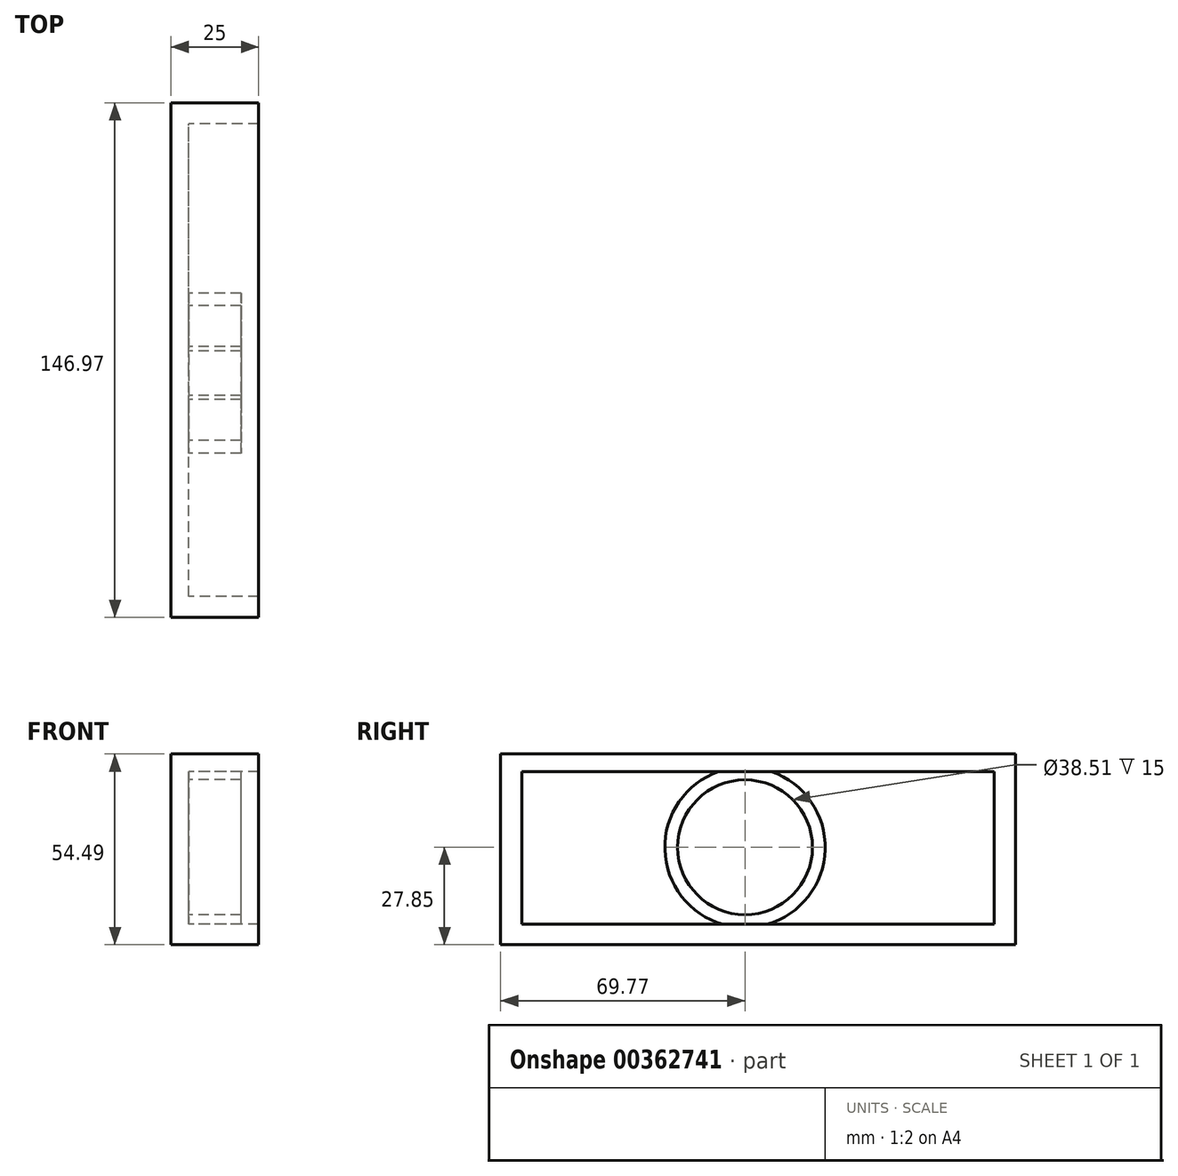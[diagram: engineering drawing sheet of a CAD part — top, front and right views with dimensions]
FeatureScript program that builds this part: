
annotation { "Feature Type Name" : "Feature", "Feature Type Description" : "" }
export const myFeature = defineFeature(function(context is Context, id is Id, definition is map)
    precondition{}
    {
        {
            var Q0;
            Q0=qCreatedBy(makeId("Right.planeOp"),FACE);
            var sketch = newSketch(context, id + "F0", { "sketchPlane" : qUnion([Q0])});
            skCircle(sketch, "E0", {"center": v(0, 0) * mm, "radius": 22.9 * mm});
            skCircle(sketch, "E1", {"center": v(0, 0) * mm, "radius": 19.25 * mm});
            skSolve(sketch);
        }
        {
            var Q0;
            Q0=makeQuery(id+"F0.imprint","IMPRINT",FACE,{"disambiguationData":[TD([[makeQuery(id+"F0.imprint","IMPRINT",EDGE,{"derivedFrom":sQuery(id+"F0.wireOp",EDGE,"E0")}),1.0]])]});
            extrude(context, id + "F1", {"entities" : qUnion([Q0]), "depth" : 20 * mm});
        }
        {
            var Q0;
            Q0=qCreatedBy(makeId("Right.planeOp"),FACE);
            var sketch = newSketch(context, id + "F2", { "sketchPlane" : qUnion([Q0])});
            skLineSegment(sketch, "E2.bottom", {"start": v(-69.77, 26.64) * mm, "end": v(77.2, 26.64) * mm});
            skLineSegment(sketch, "E2.top", {"start": v(-69.77, -27.85) * mm, "end": v(77.2, -27.85) * mm});
            skLineSegment(sketch, "E2.left", {"start": v(-69.77, 26.64) * mm, "end": v(-69.77, -27.85) * mm});
            skLineSegment(sketch, "E2.right", {"start": v(77.2, 26.64) * mm, "end": v(77.2, -27.85) * mm});
            skLineSegment(sketch, "E3.bottom", {"start": v(-63.73, 21.61) * mm, "end": v(71.17, 21.61) * mm});
            skLineSegment(sketch, "E3.top", {"start": v(-63.73, -22.02) * mm, "end": v(71.17, -22.02) * mm});
            skLineSegment(sketch, "E3.left", {"start": v(-63.73, 21.61) * mm, "end": v(-63.73, -22.02) * mm});
            skLineSegment(sketch, "E3.right", {"start": v(71.17, 21.61) * mm, "end": v(71.17, -22.02) * mm});
            skSolve(sketch);
        }
        {
            var Q0;
            Q0 = qSketchRegion(id + "F2", true);
            extrude(context, id + "F3", {"entities" : qUnion([Q0]), "depth" : 25 * mm});
        }
        {
            var Q0;
            Q0=makeQuery(id+"F2.imprint","IMPRINT",FACE,{"disambiguationData":[TD([[makeQuery(id+"F2.imprint","IMPRINT",EDGE,{"derivedFrom":sQuery(id+"F2.wireOp",EDGE,"E3.bottom")}),-1.0]])]});
            extrude(context, id + "F4", {"entities" : qUnion([Q0]), "operationType" : NewBodyOperationType.ADD, "depth" : 5 * mm});
        }
        {
            var Q0;
            Q0=qCreatedBy(makeId("Right.planeOp"),FACE);
            var sketch = newSketch(context, id + "F5", { "sketchPlane" : qUnion([Q0])});
            skLineSegment(sketch, "E4.bottom", {"start": v(-14.8, 11.53) * mm, "end": v(5.74, 11.53) * mm});
            skLineSegment(sketch, "E4.top", {"start": v(-14.8, -9.02) * mm, "end": v(5.74, -9.02) * mm});
            skLineSegment(sketch, "E4.left", {"start": v(-14.8, 11.53) * mm, "end": v(-14.8, -9.02) * mm});
            skLineSegment(sketch, "E4.right", {"start": v(5.74, 11.53) * mm, "end": v(5.74, -9.02) * mm});
            skLineSegment(sketch, "E5", {"start": v(-14.8, 11.53) * mm, "end": v(-12.6, 9.33) * mm});
            skLineSegment(sketch, "E6", {"start": v(-12.6, 9.33) * mm, "end": v(3.64, -6.72) * mm});
            skLineSegment(sketch, "E7", {"start": v(3.64, -6.72) * mm, "end": v(5.74, -9.02) * mm});
            skLineSegment(sketch, "E8.bottom", {"start": v(-12.6, 9.33) * mm, "end": v(3.64, 9.33) * mm});
            skLineSegment(sketch, "E8.top", {"start": v(-12.6, -6.72) * mm, "end": v(3.64, -6.72) * mm});
            skLineSegment(sketch, "E8.left", {"start": v(-12.6, 9.33) * mm, "end": v(-12.6, -6.72) * mm});
            skLineSegment(sketch, "E8.right", {"start": v(3.64, 9.33) * mm, "end": v(3.64, -6.72) * mm});
            skLineSegment(sketch, "E9", {"start": v(-12.6, 9.33) * mm, "end": v(-8.96, 5.73) * mm});
            skLineSegment(sketch, "E10", {"start": v(-8.96, 5.73) * mm, "end": v(0, -3.13) * mm});
            skLineSegment(sketch, "E11", {"start": v(0, -3.13) * mm, "end": v(3.64, -6.72) * mm});
            skLineSegment(sketch, "E12.bottom", {"start": v(-8.96, 5.73) * mm, "end": v(0, 5.73) * mm});
            skLineSegment(sketch, "E12.top", {"start": v(-8.96, -3.13) * mm, "end": v(0, -3.13) * mm});
            skLineSegment(sketch, "E12.left", {"start": v(-8.96, 5.73) * mm, "end": v(-8.96, -3.13) * mm});
            skLineSegment(sketch, "E12.right", {"start": v(0, 5.73) * mm, "end": v(0, -3.13) * mm});
            skSolve(sketch);
        }
        {
            var Q0;
            Q0=makeQuery(id+"F5.imprint","IMPRINT",FACE,{"disambiguationData":[TD([[makeQuery(id+"F5.imprint","IMPRINT",EDGE,{"derivedFrom":sQuery(id+"F5.wireOp",EDGE,"E4.bottom")}),-1.0]])]});
            var Q1;
            Q1=makeQuery(id+"F5.imprint","IMPRINT",FACE,{"disambiguationData":[TD([[makeQuery(id+"F5.imprint","IMPRINT",EDGE,{"derivedFrom":sQuery(id+"F5.wireOp",EDGE,"E4.top")}),1.0]])]});
            extrude(context, id + "F6", {"entities" : qUnion([Q0, Q1]), "depth" : 2 * mm});
        }
        {
            var Q0;
            Q0=makeQuery(id+"F5.imprint","IMPRINT",FACE,{"disambiguationData":[TD([[makeQuery(id+"F5.imprint","IMPRINT",EDGE,{"derivedFrom":sQuery(id+"F5.wireOp",EDGE,"E8.bottom")}),-1.0]])]});
            var Q1;
            Q1=makeQuery(id+"F5.imprint","IMPRINT",FACE,{"disambiguationData":[TD([[makeQuery(id+"F5.imprint","IMPRINT",EDGE,{"derivedFrom":sQuery(id+"F5.wireOp",EDGE,"E8.top")}),1.0]])]});
            extrude(context, id + "F7", {"entities" : qUnion([Q0, Q1]), "operationType" : NewBodyOperationType.ADD, "depth" : 4 * mm});
        }
    });
